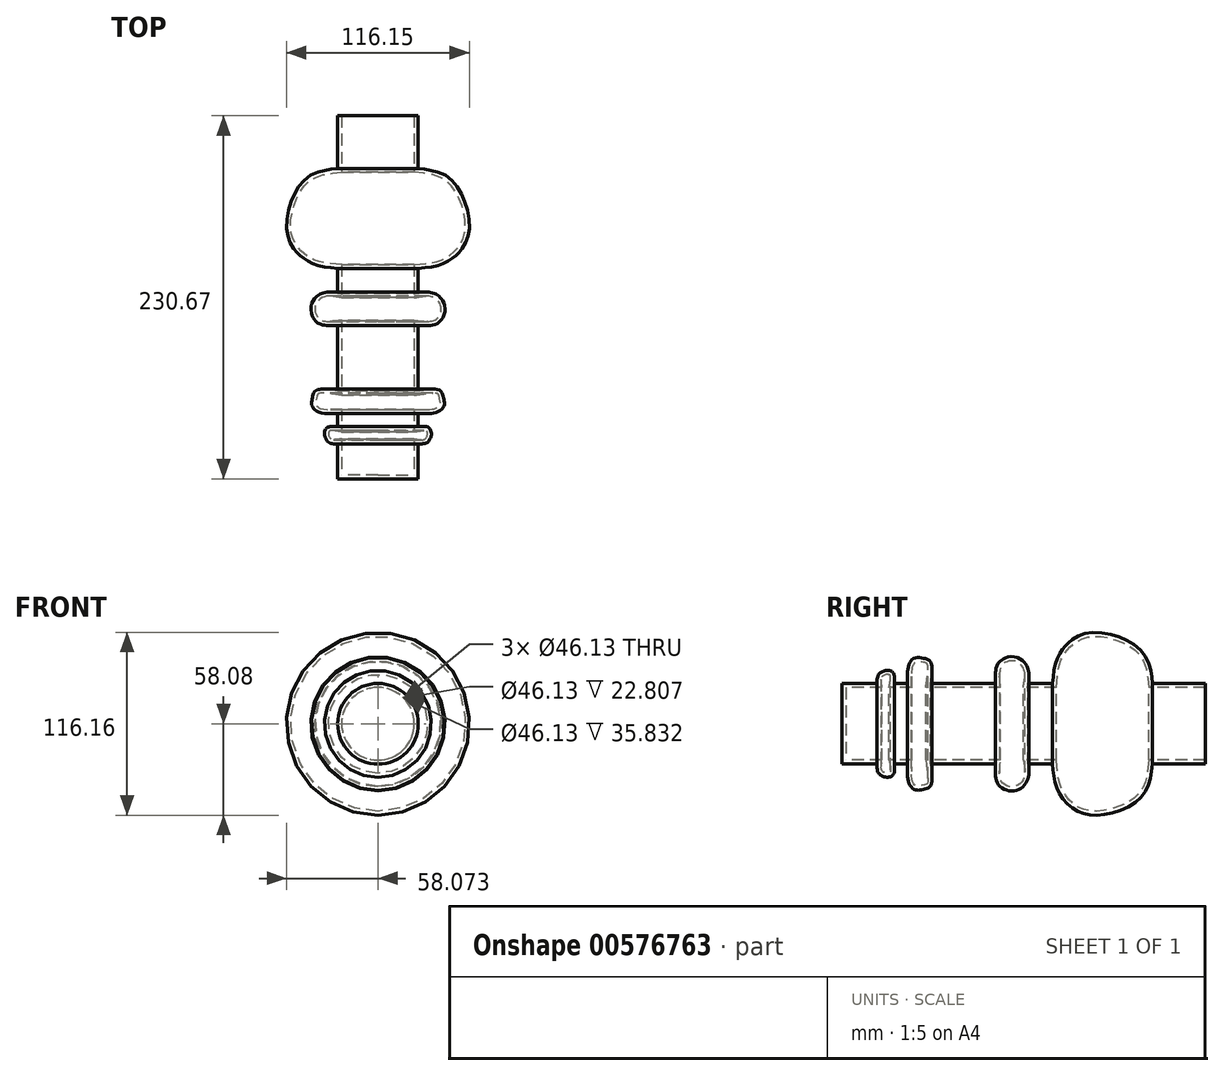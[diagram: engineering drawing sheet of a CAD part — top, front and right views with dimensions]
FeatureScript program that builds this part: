
annotation { "Feature Type Name" : "Feature", "Feature Type Description" : "" }
export const myFeature = defineFeature(function(context is Context, id is Id, definition is map)
    precondition{}
    {
        {
            var Q0;
            Q0=qCreatedBy(makeId("Top.planeOp"),FACE);
            var sketch = newSketch(context, id + "F0", { "sketchPlane" : qUnion([Q0])});
            skLineSegment(sketch, "E0", {"start": v(-161.6, -110.33) * mm, "end": v(-161.6, 64.98) * mm});
            skLineSegment(sketch, "E1", {"start": v(-161.6, 64.98) * mm, "end": v(-136, 64.98) * mm});
            skLineSegment(sketch, "E2", {"start": v(-136, 64.98) * mm, "end": v(-136, 31.42) * mm});
            skFitSpline(sketch, "E3", {"points": [v(-136, 31.42) * mm, v(-115.81, 25) * mm, v(-103.86, 0) * mm, v(-107.29, -18.26) * mm, v(-120.67, -29.2) * mm, v(-136, -31.97) * mm], "startDerivative": vector(105.63, -11.8) * mm, "endDerivative": vector(-87.67, -6.44) * mm});
            skLineSegment(sketch, "E4", {"start": v(-136, -31.97) * mm, "end": v(-136, -47.62) * mm});
            skFitSpline(sketch, "E5", {"points": [v(-136, -47.62) * mm, v(-126.66, -47.62) * mm, v(-119.22, -55.47) * mm, v(-122.98, -66.38) * mm, v(-136, -67.87) * mm], "startDerivative": vector(41.08, 6.89) * mm, "endDerivative": vector(-54.08, 5.04) * mm});
            skLineSegment(sketch, "E6", {"start": v(-136, -67.87) * mm, "end": v(-136, -109.6) * mm});
            skFitSpline(sketch, "E7", {"points": [v(-136, -109.6) * mm, v(-122.14, -109.6) * mm, v(-119.92, -114.41) * mm, v(-119.6, -118.97) * mm, v(-123.7, -123.15) * mm, v(-136, -124.15) * mm], "startDerivative": vector(64.6, 9.53) * mm, "endDerivative": vector(-55.19, 2.02) * mm});
            skFitSpline(sketch, "E8", {"points": [v(-161.6, -110.33) * mm, v(-161.6, -141.96) * mm], "startDerivative": vector(0, -31.63) * mm, "endDerivative": vector(0, -31.63) * mm});
            skLineSegment(sketch, "E9", {"start": v(-136, -124.15) * mm, "end": v(-136, -132.82) * mm});
            skFitSpline(sketch, "E10", {"points": [v(-136, -132.82) * mm, v(-129.98, -132.82) * mm, v(-127.64, -136.89) * mm, v(-130.56, -142.68) * mm, v(-136, -143.2) * mm], "startDerivative": vector(25.72, 4.41) * mm, "endDerivative": vector(-23.7, 2.85) * mm});
            skLineSegment(sketch, "E11", {"start": v(-136, -143.2) * mm, "end": v(-136, -165.7) * mm});
            skLineSegment(sketch, "E12", {"start": v(-136, -165.7) * mm, "end": v(-161.6, -165.7) * mm});
            skLineSegment(sketch, "E13", {"start": v(-161.6, -165.7) * mm, "end": v(-161.6, -141.96) * mm});
            skPoint(sketch, "E14", {"position": v(-136, 4.83) * mm});
            skPoint(sketch, "E15", {"position": v(-128.63, 0) * mm});
            skPoint(sketch, "E16", {"position": v(-143.78, -5.51) * mm});
            skSolve(sketch);
        }
        {
            var Q0;
            Q0=makeQuery(id+"F0.imprint","IMPRINT",FACE,{"disambiguationData":[TD([[makeQuery(id+"F0.imprint","IMPRINT",EDGE,{"derivedFrom":sQuery(id+"F0.wireOp",EDGE,"E0")}),-1.0]])]});
            var Q1;
            Q1=sQuery(id+"F0.wireOp",EDGE,"E13");
            revolve(context, id + "F1", {"entities" : qUnion([Q0]), "axis" : qUnion([Q1]), "revolveType" : RevolveType.FULL});
        }
        {
            var Q0;
            Q0=makeQuery(id+"F1.opRevolve","SWEPT_FACE",FACE,{"disambiguationData":[OSD([sQuery(id+"F0.wireOp",EDGE,"E1")])]});
            shell(context, id + "F2", {"entities" : qUnion([Q0]), "thickness" : 2.54 * mm});
        }
    });
